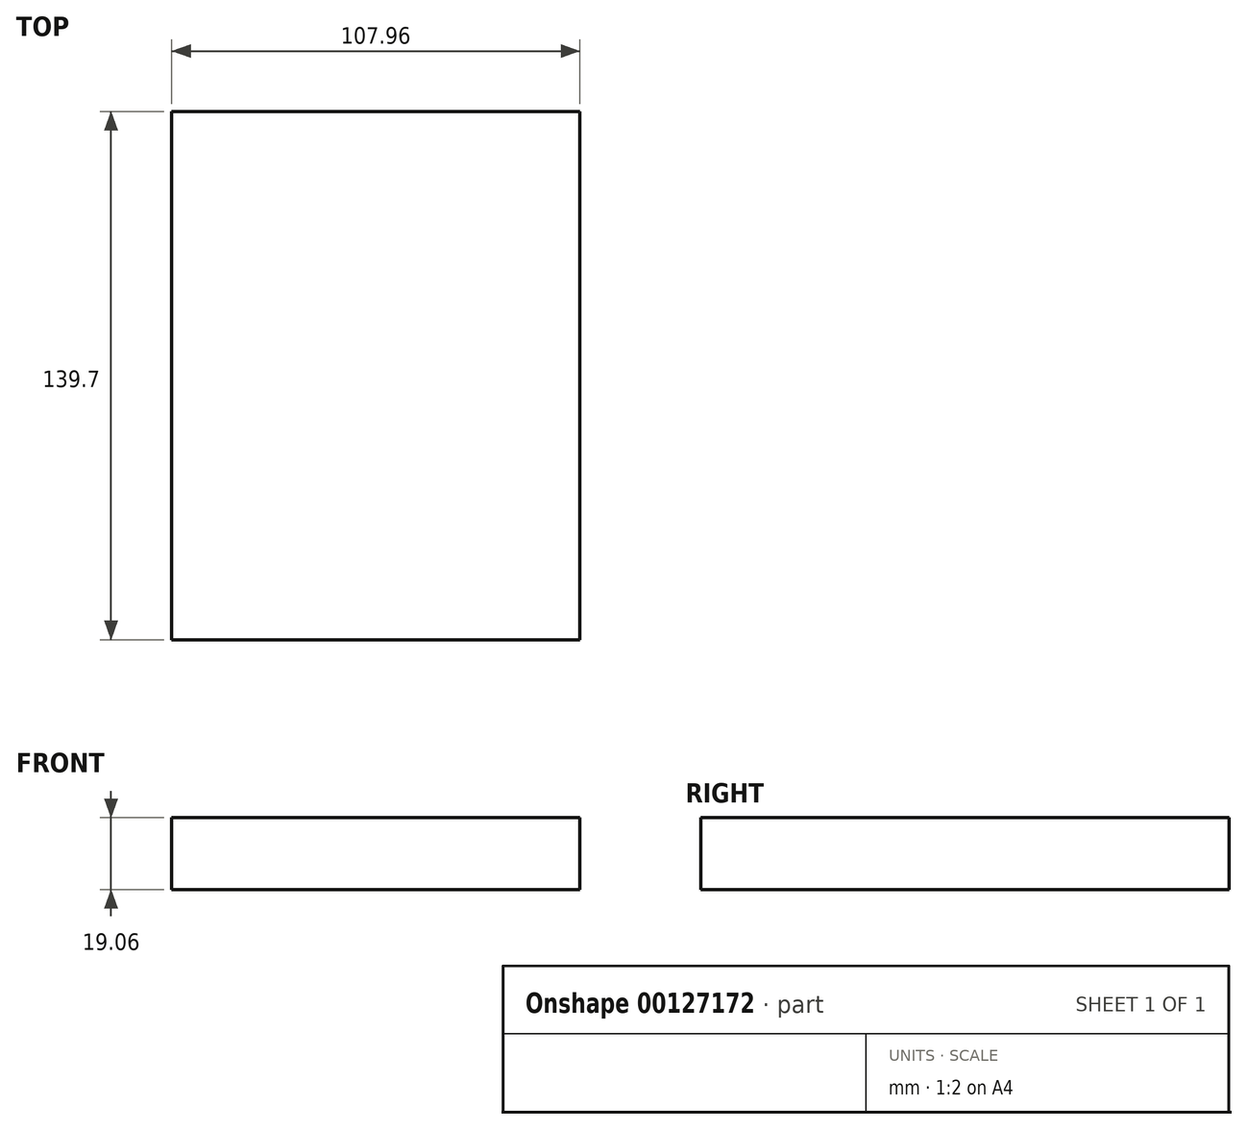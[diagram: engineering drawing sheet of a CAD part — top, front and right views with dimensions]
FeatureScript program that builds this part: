
annotation { "Feature Type Name" : "Feature", "Feature Type Description" : "" }
export const myFeature = defineFeature(function(context is Context, id is Id, definition is map)
    precondition{}
    {
        {
            var Q0;
            Q0=qCreatedBy(makeId("Front.planeOp"),FACE);
            var sketch = newSketch(context, id + "F0", { "sketchPlane" : qUnion([Q0])});
            skLineSegment(sketch, "E0.bottom", {"start": v(53.98, -9.52) * mm, "end": v(-53.98, -9.52) * mm});
            skLineSegment(sketch, "E0.top", {"start": v(53.98, 9.53) * mm, "end": v(-53.98, 9.52) * mm});
            skLineSegment(sketch, "E0.left", {"start": v(53.98, -9.52) * mm, "end": v(53.98, 9.53) * mm});
            skLineSegment(sketch, "E0.right", {"start": v(-53.98, -9.52) * mm, "end": v(-53.98, 9.53) * mm});
            skPoint(sketch, "E0.middle", {"position": v(0, 0) * mm});
            skSolve(sketch);
        }
        {
            var Q0;
            Q0=qSketchRegion(id+"F0",true);
            extrude(context, id + "F1", {"entities" : qUnion([Q0]), "depth" : 139.7 * mm});
        }
    });
